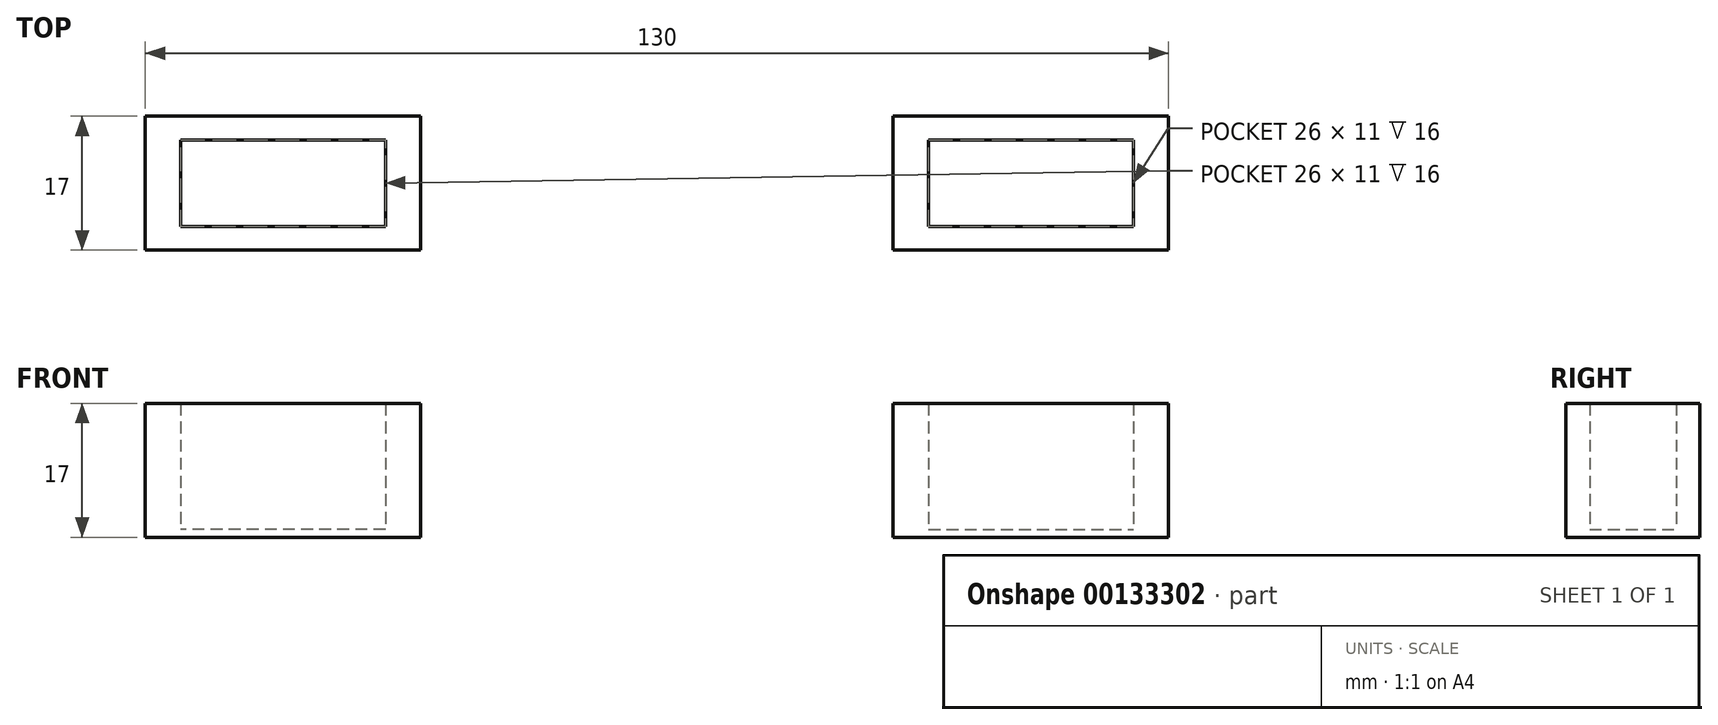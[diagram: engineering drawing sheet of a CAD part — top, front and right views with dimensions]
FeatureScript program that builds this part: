
annotation { "Feature Type Name" : "Feature", "Feature Type Description" : "" }
export const myFeature = defineFeature(function(context is Context, id is Id, definition is map)
    precondition{}
    {
        {
            var Q0;
            Q0=qCreatedBy(makeId("Top.planeOp"),FACE);
            var sketch = newSketch(context, id + "F0", { "sketchPlane" : qUnion([Q0])});
            skLineSegment(sketch, "E0.bottom", {"start": v(17.5, -8.5) * mm, "end": v(-17.5, -8.5) * mm});
            skLineSegment(sketch, "E0.top", {"start": v(17.5, 8.5) * mm, "end": v(-17.5, 8.5) * mm});
            skLineSegment(sketch, "E0.left", {"start": v(17.5, -8.5) * mm, "end": v(17.5, 8.5) * mm});
            skLineSegment(sketch, "E0.right", {"start": v(-17.5, -8.5) * mm, "end": v(-17.5, 8.5) * mm});
            skPoint(sketch, "E0.middle", {"position": v(0, 0) * mm});
            skLineSegment(sketch, "E1.bottom", {"start": v(13, -5.5) * mm, "end": v(-13, -5.5) * mm});
            skLineSegment(sketch, "E1.top", {"start": v(13, 5.5) * mm, "end": v(-13, 5.5) * mm});
            skLineSegment(sketch, "E1.left", {"start": v(13, -5.5) * mm, "end": v(13, 5.5) * mm});
            skLineSegment(sketch, "E1.right", {"start": v(-13, -5.5) * mm, "end": v(-13, 5.5) * mm});
            skLineSegment(sketch, "E2", {"start": v(47.5, 19.56) * mm, "end": v(47.5, -20.93) * mm, "construction": true});
            skPoint(sketch, "E3.MirrorP", {"position": v(95, 0) * mm});
            skLineSegment(sketch, "E4.MirrorCS", {"start": v(108, -5.5) * mm, "end": v(108, 5.5) * mm});
            skLineSegment(sketch, "E5.MirrorCS", {"start": v(82, -5.5) * mm, "end": v(82, 5.5) * mm});
            skLineSegment(sketch, "E6.MirrorCS", {"start": v(82, 5.5) * mm, "end": v(108, 5.5) * mm});
            skLineSegment(sketch, "E7.MirrorCS", {"start": v(82, -5.5) * mm, "end": v(108, -5.5) * mm});
            skLineSegment(sketch, "E8.MirrorCS", {"start": v(77.5, -8.5) * mm, "end": v(112.5, -8.5) * mm});
            skLineSegment(sketch, "E9.MirrorCS", {"start": v(77.5, 8.5) * mm, "end": v(112.5, 8.5) * mm});
            skLineSegment(sketch, "E10.MirrorCS", {"start": v(112.5, -8.5) * mm, "end": v(112.5, 8.5) * mm});
            skLineSegment(sketch, "E11.MirrorCS", {"start": v(77.5, -8.5) * mm, "end": v(77.5, 8.5) * mm});
            skSolve(sketch);
        }
        {
            var Q0;
            Q0=makeQuery(id+"F0.imprint","IMPRINT",FACE,{"disambiguationData":[TD([[makeQuery(id+"F0.imprint","IMPRINT",EDGE,{"derivedFrom":sQuery(id+"F0.wireOp",EDGE,"E1.bottom")}),-1.0]])]});
            extrude(context, id + "F1", {"entities" : qUnion([Q0]), "depth" : 1 * mm});
        }
        {
            var Q0;
            Q0=makeQuery(id+"F0.imprint","IMPRINT",FACE,{"disambiguationData":[TD([[makeQuery(id+"F0.imprint","IMPRINT",EDGE,{"derivedFrom":sQuery(id+"F0.wireOp",EDGE,"E0.bottom")}),-1.0]])]});
            extrude(context, id + "F2", {"entities" : qUnion([Q0]), "operationType" : NewBodyOperationType.ADD, "depth" : 17 * mm});
        }
        {
            var Q0;
            Q0=makeQuery(id+"F0.imprint","IMPRINT",FACE,{"disambiguationData":[TD([[makeQuery(id+"F0.imprint","IMPRINT",EDGE,{"derivedFrom":sQuery(id+"F0.wireOp",EDGE,"E4.MirrorCS")}),1.0]])]});
            extrude(context, id + "F3", {"entities" : qUnion([Q0]), "depth" : 1 * mm});
        }
        {
            var Q0;
            Q0=makeQuery(id+"F0.imprint","IMPRINT",FACE,{"disambiguationData":[TD([[makeQuery(id+"F0.imprint","IMPRINT",EDGE,{"derivedFrom":sQuery(id+"F0.wireOp",EDGE,"E4.MirrorCS")}),-1.0]])]});
            extrude(context, id + "F4", {"entities" : qUnion([Q0]), "operationType" : NewBodyOperationType.ADD, "depth" : 17 * mm});
        }
    });
